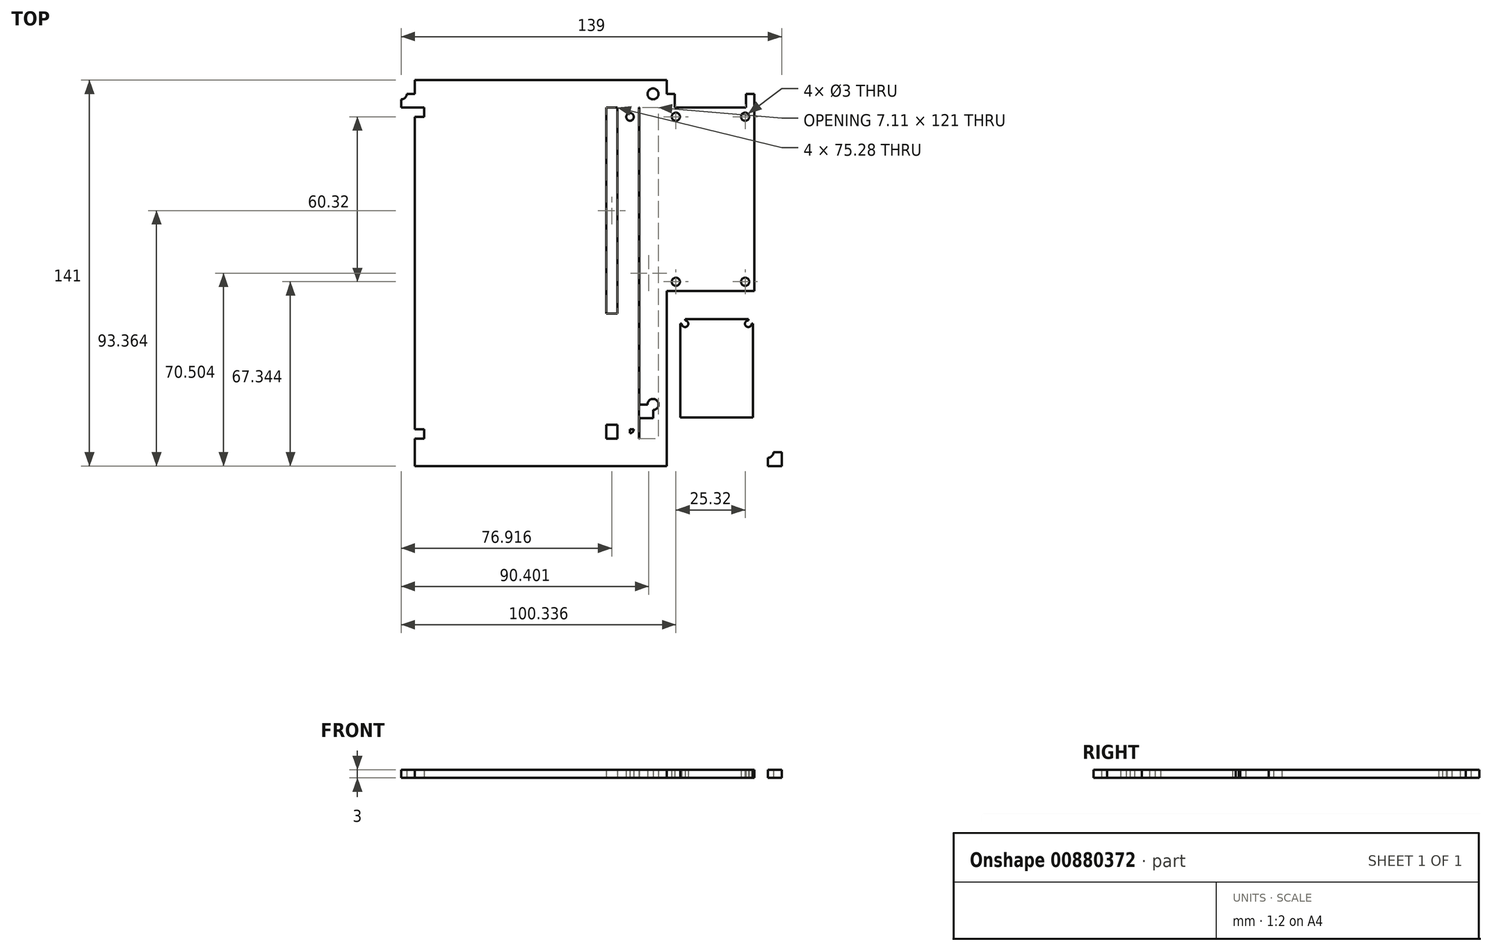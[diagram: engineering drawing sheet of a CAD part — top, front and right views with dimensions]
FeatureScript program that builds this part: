
annotation { "Feature Type Name" : "Feature", "Feature Type Description" : "" }
export const myFeature = defineFeature(function(context is Context, id is Id, definition is map)
    precondition{}
    {
        {
            var Q0;
            Q0=qCreatedBy(makeId("Top.planeOp"),FACE);
            var sketch = newSketch(context, id + "F0", { "sketchPlane" : qUnion([Q0])});
            skLineSegment(sketch, "E0.bottom", {"start": v(-139.34, -1.26) * mm, "end": v(-129.34, -1.26) * mm});
            skLineSegment(sketch, "E0.top", {"start": v(-139.34, -11.26) * mm, "end": v(-129.34, -11.26) * mm});
            skLineSegment(sketch, "E0.left", {"start": v(-139.34, -1.26) * mm, "end": v(-139.34, -11.26) * mm});
            skLineSegment(sketch, "E0.right", {"start": v(-129.34, -1.26) * mm, "end": v(-129.34, -11.26) * mm});
            skLineSegment(sketch, "E1.left", {"start": v(-129.34, -11.26) * mm, "end": v(-129.34, -114.76) * mm});
            skLineSegment(sketch, "E2.bottom", {"start": v(-124.34, -124.58) * mm, "end": v(-97.84, -124.58) * mm});
            skLineSegment(sketch, "E2.top", {"start": v(-124.34, -88.58) * mm, "end": v(-97.84, -88.58) * mm});
            skLineSegment(sketch, "E2.left", {"start": v(-124.34, -124.58) * mm, "end": v(-124.34, -88.58) * mm});
            skLineSegment(sketch, "E2.right", {"start": v(-97.84, -124.58) * mm, "end": v(-97.84, -88.58) * mm});
            skLineSegment(sketch, "E3.bottom", {"start": v(-129.34, -114.76) * mm, "end": v(-139.34, -114.76) * mm});
            skLineSegment(sketch, "E3.top", {"start": v(-129.34, -124.76) * mm, "end": v(-139.34, -124.76) * mm});
            skLineSegment(sketch, "E3.left", {"start": v(-129.34, -114.76) * mm, "end": v(-129.34, -124.76) * mm});
            skLineSegment(sketch, "E3.right", {"start": v(-139.34, -114.76) * mm, "end": v(-139.34, -124.76) * mm});
            skLineSegment(sketch, "E4", {"start": v(-129.34, -11.26) * mm, "end": v(-126, -11.26) * mm});
            skLineSegment(sketch, "E5.bottom", {"start": v(-129.34, -11.26) * mm, "end": v(-126.54, -11.26) * mm});
            skLineSegment(sketch, "E5.left", {"start": v(-129.34, -11.26) * mm, "end": v(-129.34, -14.06) * mm});
            skLineSegment(sketch, "E6.left", {"start": v(-129.34, -114.76) * mm, "end": v(-129.34, -111.76) * mm});
            skLineSegment(sketch, "E7.bottom", {"start": v(-97.84, -88.58) * mm, "end": v(-99.54, -88.58) * mm});
            skLineSegment(sketch, "E7.top", {"start": v(-97.84, -90.28) * mm, "end": v(-99.54, -90.28) * mm});
            skLineSegment(sketch, "E7.left", {"start": v(-97.84, -88.58) * mm, "end": v(-97.84, -90.28) * mm});
            skLineSegment(sketch, "E7.right", {"start": v(-99.54, -88.58) * mm, "end": v(-99.54, -90.28) * mm});
            skLineSegment(sketch, "E8.bottom", {"start": v(-124.34, -88.58) * mm, "end": v(-122.64, -88.58) * mm});
            skLineSegment(sketch, "E8.top", {"start": v(-124.34, -90.28) * mm, "end": v(-122.64, -90.28) * mm});
            skLineSegment(sketch, "E8.left", {"start": v(-124.34, -88.58) * mm, "end": v(-124.34, -90.28) * mm});
            skLineSegment(sketch, "E8.right", {"start": v(-122.64, -88.58) * mm, "end": v(-122.64, -90.28) * mm});
            skCircle(sketch, "E9", {"center": v(-122.64, -90.28) * mm, "radius": 1.2 * mm});
            skCircle(sketch, "E10", {"center": v(-99.54, -90.28) * mm, "radius": 1.2 * mm});
            skLineSegment(sketch, "E11.bottom", {"start": v(-139.34, -124.76) * mm, "end": v(-134.34, -124.76) * mm});
            skLineSegment(sketch, "E11.top", {"start": v(-139.34, -119.76) * mm, "end": v(-134.34, -119.76) * mm});
            skLineSegment(sketch, "E11.left", {"start": v(-139.34, -124.76) * mm, "end": v(-139.34, -119.76) * mm});
            skLineSegment(sketch, "E11.right", {"start": v(-134.34, -124.76) * mm, "end": v(-134.34, -119.76) * mm});
            skCircle(sketch, "E12", {"center": v(-134.34, -119.76) * mm, "radius": 2 * mm});
            skLineSegment(sketch, "E13.bottom", {"start": v(-139.34, -1.26) * mm, "end": v(-134.34, -1.26) * mm});
            skLineSegment(sketch, "E13.top", {"start": v(-139.34, -6.26) * mm, "end": v(-134.34, -6.26) * mm});
            skLineSegment(sketch, "E13.left", {"start": v(-139.34, -1.26) * mm, "end": v(-139.34, -6.26) * mm});
            skLineSegment(sketch, "E13.right", {"start": v(-134.34, -1.26) * mm, "end": v(-134.34, -6.26) * mm});
            skCircle(sketch, "E14", {"center": v(-134.34, -6.26) * mm, "radius": 2 * mm});
            skLineSegment(sketch, "E15.bottom", {"start": v(-129.34, -11.26) * mm, "end": v(-126.34, -11.26) * mm});
            skLineSegment(sketch, "E15.left", {"start": v(-129.34, -11.26) * mm, "end": v(-129.34, -27.96) * mm});
            skLineSegment(sketch, "E16.left", {"start": v(-129.34, -114.76) * mm, "end": v(-129.34, -108.76) * mm});
            skLineSegment(sketch, "E17.left", {"start": v(-129.34, -114.76) * mm, "end": v(-129.34, -27.46) * mm});
            skLineSegment(sketch, "E18.MirrorCS", {"start": v(-139.5, -132.26) * mm, "end": v(-139.5, -11.26) * mm});
            skLineSegment(sketch, "E19.MirrorCS", {"start": v(-221.34, -11.26) * mm, "end": v(-139.34, -11.26) * mm});
            skLineSegment(sketch, "E20.MirrorCS", {"start": v(-221.34, -132.26) * mm, "end": v(-139.34, -132.26) * mm});
            skCircle(sketch, "E21.MirrorC", {"center": v(-142.74, -128.86) * mm, "radius": 1.4 * mm});
            skCircle(sketch, "E22.MirrorC", {"center": v(-217.94, -128.86) * mm, "radius": 1.7 * mm});
            skCircle(sketch, "E23.MirrorC", {"center": v(-217.94, -14.66) * mm, "radius": 1.4 * mm});
            skCircle(sketch, "E24.MirrorC", {"center": v(-142.74, -14.66) * mm, "radius": 1.4 * mm});
            skLineSegment(sketch, "E25.MirrorCS", {"start": v(-142.74, -11.26) * mm, "end": v(-142.74, -14.66) * mm});
            skLineSegment(sketch, "E26.MirrorCS", {"start": v(-139.34, -14.66) * mm, "end": v(-142.74, -14.66) * mm});
            skLineSegment(sketch, "E27.MirrorCS", {"start": v(-217.94, -11.26) * mm, "end": v(-217.94, -14.66) * mm});
            skLineSegment(sketch, "E28.MirrorCS", {"start": v(-221.34, -14.66) * mm, "end": v(-217.94, -14.66) * mm});
            skLineSegment(sketch, "E29.MirrorCS", {"start": v(-142.74, -132.26) * mm, "end": v(-142.74, -128.86) * mm});
            skLineSegment(sketch, "E30.MirrorCS", {"start": v(-139.34, -128.86) * mm, "end": v(-142.74, -128.86) * mm});
            skLineSegment(sketch, "E31.MirrorCS", {"start": v(-221.34, -128.86) * mm, "end": v(-217.94, -128.86) * mm});
            skLineSegment(sketch, "E32.MirrorCS", {"start": v(-217.94, -132.26) * mm, "end": v(-217.94, -128.86) * mm});
            skLineSegment(sketch, "E33", {"start": v(-221.34, -11.26) * mm, "end": v(-221.34, -1.26) * mm});
            skLineSegment(sketch, "E34", {"start": v(-221.34, -132.26) * mm, "end": v(-221.34, -11.26) * mm});
            skLineSegment(sketch, "E35", {"start": v(-221.34, -132.26) * mm, "end": v(-231.5, -132.26) * mm});
            skLineSegment(sketch, "E36.bottom", {"start": v(-221.34, -132.26) * mm, "end": v(-231.34, -132.26) * mm});
            skLineSegment(sketch, "E36.top", {"start": v(-221.34, -142.26) * mm, "end": v(-231.34, -142.26) * mm});
            skLineSegment(sketch, "E36.left", {"start": v(-221.34, -132.26) * mm, "end": v(-221.34, -142.26) * mm});
            skLineSegment(sketch, "E36.right", {"start": v(-231.34, -132.26) * mm, "end": v(-231.34, -142.26) * mm});
            skLineSegment(sketch, "E37.bottom", {"start": v(-221.34, -142.26) * mm, "end": v(-139.34, -142.26) * mm});
            skLineSegment(sketch, "E37.left", {"start": v(-221.34, -142.26) * mm, "end": v(-221.34, -132.26) * mm});
            skLineSegment(sketch, "E38", {"start": v(-231.34, -132.26) * mm, "end": v(-231.34, -1.26) * mm});
            skLineSegment(sketch, "E39.bottom", {"start": v(-129.34, -124.76) * mm, "end": v(-139.2, -124.76) * mm});
            skLineSegment(sketch, "E39.top", {"start": v(-129.34, -142.26) * mm, "end": v(-139.34, -142.26) * mm});
            skLineSegment(sketch, "E39.left", {"start": v(-129.34, -124.76) * mm, "end": v(-129.34, -142.26) * mm});
            skLineSegment(sketch, "E40", {"start": v(-139.34, -142.26) * mm, "end": v(-139.5, -132.26) * mm});
            skLineSegment(sketch, "E41.bottom", {"start": v(-231.34, -142.26) * mm, "end": v(-226.34, -142.26) * mm});
            skLineSegment(sketch, "E41.top", {"start": v(-231.34, -137.4) * mm, "end": v(-226.34, -137.4) * mm});
            skLineSegment(sketch, "E41.left", {"start": v(-231.34, -142.26) * mm, "end": v(-231.34, -137.4) * mm});
            skLineSegment(sketch, "E41.right", {"start": v(-226.34, -142.26) * mm, "end": v(-226.34, -137.4) * mm});
            skCircle(sketch, "E42", {"center": v(-226.34, -137.4) * mm, "radius": 2 * mm});
            skLineSegment(sketch, "E43.bottom", {"start": v(-221.34, -11.26) * mm, "end": v(-226.34, -11.26) * mm});
            skLineSegment(sketch, "E43.top", {"start": v(-221.34, -6.26) * mm, "end": v(-226.34, -6.26) * mm});
            skLineSegment(sketch, "E43.left", {"start": v(-221.34, -11.26) * mm, "end": v(-221.34, -6.26) * mm});
            skLineSegment(sketch, "E43.right", {"start": v(-226.34, -11.26) * mm, "end": v(-226.34, -6.26) * mm});
            skCircle(sketch, "E44", {"center": v(-226.34, -6.26) * mm, "radius": 2 * mm});
            skLineSegment(sketch, "E45.bottom", {"start": v(-129.34, -142.26) * mm, "end": v(-87.34, -142.26) * mm});
            skLineSegment(sketch, "E45.left", {"start": v(-129.34, -142.26) * mm, "end": v(-129.34, -114.76) * mm});
            skLineSegment(sketch, "E46.bottom", {"start": v(-139.34, -132.26) * mm, "end": v(-151.42, -132.26) * mm});
            skLineSegment(sketch, "E46.top", {"start": v(-139.34, -11.26) * mm, "end": v(-151.42, -11.26) * mm});
            skLineSegment(sketch, "E46.left", {"start": v(-139.34, -132.26) * mm, "end": v(-139.34, -11.26) * mm});
            skLineSegment(sketch, "E46.right", {"start": v(-151.42, -132.26) * mm, "end": v(-151.42, -11.26) * mm});
            skLineSegment(sketch, "E47.bottom", {"start": v(-151.42, -132.26) * mm, "end": v(-147.42, -132.26) * mm});
            skLineSegment(sketch, "E47.top", {"start": v(-151.42, -11.26) * mm, "end": v(-147.42, -11.26) * mm});
            skLineSegment(sketch, "E47.right", {"start": v(-147.42, -132.26) * mm, "end": v(-147.42, -11.26) * mm});
            skLineSegment(sketch, "E48.top", {"start": v(-151.42, -127.18) * mm, "end": v(-147.42, -127.18) * mm});
            skLineSegment(sketch, "E48.left", {"start": v(-151.42, -132.26) * mm, "end": v(-151.42, -127.18) * mm});
            skLineSegment(sketch, "E48.right", {"start": v(-147.42, -132.26) * mm, "end": v(-147.42, -127.18) * mm});
            skLineSegment(sketch, "E49.top", {"start": v(-151.42, -86.54) * mm, "end": v(-147.42, -86.54) * mm});
            skLineSegment(sketch, "E49.left", {"start": v(-151.42, -127.18) * mm, "end": v(-151.42, -86.54) * mm});
            skLineSegment(sketch, "E49.right", {"start": v(-147.42, -127.18) * mm, "end": v(-147.42, -86.54) * mm});
            skLineSegment(sketch, "E50.bottom", {"start": v(-129.34, -11.26) * mm, "end": v(-97.34, -11.26) * mm});
            skLineSegment(sketch, "E50.top", {"start": v(-129.34, -78.26) * mm, "end": v(-97.34, -78.26) * mm});
            skLineSegment(sketch, "E50.left", {"start": v(-129.34, -11.26) * mm, "end": v(-129.34, -78.26) * mm});
            skLineSegment(sketch, "E50.right", {"start": v(-97.34, -11.26) * mm, "end": v(-97.34, -78.26) * mm});
            skLineSegment(sketch, "E51.bottom", {"start": v(-129.34, -78.26) * mm, "end": v(-126, -78.26) * mm});
            skLineSegment(sketch, "E51.left", {"start": v(-129.34, -78.26) * mm, "end": v(-129.34, -74.92) * mm});
            skLineSegment(sketch, "E52.bottom", {"start": v(-97.34, -78.26) * mm, "end": v(-100.68, -78.26) * mm});
            skLineSegment(sketch, "E52.left", {"start": v(-97.34, -78.26) * mm, "end": v(-97.34, -74.92) * mm});
            skLineSegment(sketch, "E53.left", {"start": v(-129.34, -11.26) * mm, "end": v(-129.34, -14.6) * mm});
            skLineSegment(sketch, "E54.bottom", {"start": v(-97.34, -11.26) * mm, "end": v(-100.68, -11.26) * mm});
            skLineSegment(sketch, "E54.left", {"start": v(-97.34, -11.26) * mm, "end": v(-97.34, -14.6) * mm});
            skCircle(sketch, "E55", {"center": v(-126, -74.92) * mm, "radius": 1.5 * mm});
            skCircle(sketch, "E56", {"center": v(-100.68, -74.92) * mm, "radius": 1.5 * mm});
            skCircle(sketch, "E57", {"center": v(-100.68, -14.6) * mm, "radius": 1.5 * mm});
            skCircle(sketch, "E58", {"center": v(-126, -14.6) * mm, "radius": 1.5 * mm});
            skLineSegment(sketch, "E59", {"start": v(-231.34, -1.26) * mm, "end": v(-139.34, -1.26) * mm});
            skLineSegment(sketch, "E60", {"start": v(-87.34, -1.26) * mm, "end": v(-87.34, -142.26) * mm});
            skLineSegment(sketch, "E61.top", {"start": v(-129.34, -6.26) * mm, "end": v(-97.34, -6.26) * mm});
            skLineSegment(sketch, "E61.left", {"start": v(-129.34, -11.26) * mm, "end": v(-129.34, -6.26) * mm});
            skLineSegment(sketch, "E61.right", {"start": v(-97.34, -11.26) * mm, "end": v(-97.34, -6.26) * mm});
            skLineSegment(sketch, "E62", {"start": v(-87.34, -1.26) * mm, "end": v(-129.34, -1.26) * mm});
            skLineSegment(sketch, "E63.top", {"start": v(-129.34, -6.26) * mm, "end": v(-126.34, -6.26) * mm});
            skLineSegment(sketch, "E63.right", {"start": v(-126.34, -11.26) * mm, "end": v(-126.34, -6.26) * mm});
            skLineSegment(sketch, "E64.right", {"start": v(-97.34, -11.26) * mm, "end": v(-97.34, -11.26) * mm});
            skLineSegment(sketch, "E65.bottom", {"start": v(-97.34, -11.26) * mm, "end": v(-100.34, -11.26) * mm});
            skLineSegment(sketch, "E65.top", {"start": v(-97.34, -6.26) * mm, "end": v(-100.34, -6.26) * mm});
            skLineSegment(sketch, "E65.right", {"start": v(-100.34, -11.26) * mm, "end": v(-100.34, -6.26) * mm});
            skLineSegment(sketch, "E66.bottom", {"start": v(-87.34, -142.26) * mm, "end": v(-92.34, -142.26) * mm});
            skLineSegment(sketch, "E66.top", {"start": v(-87.34, -137.26) * mm, "end": v(-92.34, -137.26) * mm});
            skLineSegment(sketch, "E66.left", {"start": v(-87.34, -142.26) * mm, "end": v(-87.34, -137.26) * mm});
            skLineSegment(sketch, "E66.right", {"start": v(-92.34, -142.26) * mm, "end": v(-92.34, -137.26) * mm});
            skLineSegment(sketch, "E67.bottom", {"start": v(-87.34, -1.26) * mm, "end": v(-92.34, -1.26) * mm});
            skLineSegment(sketch, "E67.top", {"start": v(-87.34, -6.26) * mm, "end": v(-92.34, -6.26) * mm});
            skLineSegment(sketch, "E67.left", {"start": v(-87.34, -1.26) * mm, "end": v(-87.34, -6.26) * mm});
            skLineSegment(sketch, "E67.right", {"start": v(-92.34, -1.26) * mm, "end": v(-92.34, -6.26) * mm});
            skCircle(sketch, "E68", {"center": v(-92.34, -137.26) * mm, "radius": 2 * mm});
            skCircle(sketch, "E69", {"center": v(-92.34, -6.26) * mm, "radius": 2 * mm});
            skSolve(sketch);
        }
        {
            var Q0;
            Q0=makeQuery(id+"F0.imprint","IMPRINT",FACE,{"disambiguationData":[TD([[makeQuery(id+"F0.imprint","IMPRINT",EDGE,{"derivedFrom":sQuery(id+"F0.wireOp",EDGE,"E1.right")}),1.0]])]});
            var Q1;
            Q1=makeQuery(id+"F0.imprint","IMPRINT",FACE,{"disambiguationData":[TD([[makeQuery(id+"F0.imprint","IMPRINT",EDGE,{"derivedFrom":sQuery(id+"F0.wireOp",EDGE,"5LbS737s-GMt0-3yRV-RusY-74rPWMoJnLPp.bottom")}),-1.0]])]});
            var Q2;
            Q2=makeQuery(id+"F0.imprint","IMPRINT",FACE,{"disambiguationData":[TD([[makeQuery(id+"F0.imprint","IMPRINT",EDGE,{"derivedFrom":sQuery(id+"F0.wireOp",EDGE,"E1.top")}),-1.0]])]});
            var Q3;
            Q3=makeQuery(id+"F0.imprint","IMPRINT",FACE,{"disambiguationData":[TD([[makeQuery(id+"F0.imprint","IMPRINT",EDGE,{"derivedFrom":sQuery(id+"F0.wireOp",EDGE,"E3.bottom")}),1.0]])]});
            var Q4;
            Q4=makeQuery(id+"F0.imprint","IMPRINT",FACE,{"disambiguationData":[TD([[makeQuery(id+"F0.imprint","IMPRINT",EDGE,{"derivedFrom":sQuery(id+"F0.wireOp",EDGE,"97myMdQA-agTY-EE5a-eSU0-3Ky6piHqa90I.left")}),1.0]])]});
            var Q5;
            Q5=makeQuery(id+"F0.imprint","IMPRINT",FACE,{"disambiguationData":[TD([[makeQuery(id+"F0.imprint","IMPRINT",EDGE,{"derivedFrom":sQuery(id+"F0.wireOp",EDGE,"E0.bottom")}),-1.0]])]});
            var Q6;
            {var subQ0=sQuery(id+"F0.wireOp",EDGE,"E0.right");Q6=makeQuery(id+"F0.imprint","IMPRINT",FACE,{"disambiguationData":[TD([[makeQuery(id+"F0.imprint","IMPRINT",EDGE,{"derivedFrom":subQ0}),1.0]])]});}
            var Q7;
            {var subQ2=sQuery(id+"F0.wireOp",EDGE,"97myMdQA-agTY-EE5a-eSU0-3Ky6piHqa90I.right");Q7=makeQuery(id+"F0.imprint","IMPRINT",FACE,{"disambiguationData":[TD([[makeQuery(id+"F0.imprint","IMPRINT",EDGE,{"derivedFrom":subQ2}),-1.0]])]});}
            var Q8;
            {var subQ0=sQuery(id+"F0.wireOp",EDGE,"5LbS737s-GMt0-3yRV-RusY-74rPWMoJnLPp.top");Q8=makeQuery(id+"F0.imprint","IMPRINT",FACE,{"disambiguationData":[TD([[makeQuery(id+"F0.imprint","IMPRINT",EDGE,{"derivedFrom":subQ0}),-1.0]])]});}
            var Q9;
            {var subQ1=sQuery(id+"F0.wireOp",EDGE,"R2WY0SRa-AH7d-UwmP-SjNj-uamWJIKeu4LY.bottom");Q9=makeQuery(id+"F0.imprint","IMPRINT",FACE,{"disambiguationData":[TD([[makeQuery(id+"F0.imprint","IMPRINT",EDGE,{"derivedFrom":subQ1}),1.0]])]});}
            var Q10;
            {var subQ1=sQuery(id+"F0.wireOp",EDGE,"E11.bottom");Q10=makeQuery(id+"F0.imprint","IMPRINT",FACE,{"disambiguationData":[TD([[makeQuery(id+"F0.imprint","IMPRINT",EDGE,{"derivedFrom":subQ1}),1.0]])]});}
            var Q11;
            {var subQ1=sQuery(id+"F0.wireOp",EDGE,"E13.bottom");Q11=makeQuery(id+"F0.imprint","IMPRINT",FACE,{"disambiguationData":[TD([[makeQuery(id+"F0.imprint","IMPRINT",EDGE,{"derivedFrom":subQ1}),-1.0]])]});}
            var Q12;
            {var subQ1=sQuery(id+"F0.wireOp",EDGE,"GQXUHQXK-ggnU-ynUD-V26a-dyRAC2FfGFxX.bottom");Q12=makeQuery(id+"F0.imprint","IMPRINT",FACE,{"disambiguationData":[TD([[makeQuery(id+"F0.imprint","IMPRINT",EDGE,{"derivedFrom":subQ1}),1.0]])]});}
            var Q13;
            {var subQ1=sQuery(id+"F0.wireOp",EDGE,"E39.top");Q13=makeQuery(id+"F0.imprint","IMPRINT",FACE,{"disambiguationData":[TD([[makeQuery(id+"F0.imprint","IMPRINT",EDGE,{"derivedFrom":subQ1}),-1.0]])]});}
            var Q14;
            Q14=makeQuery(id+"F0.imprint","IMPRINT",FACE,{"disambiguationData":[TD([[makeQuery(id+"F0.imprint","IMPRINT",EDGE,{"derivedFrom":sQuery(id+"F0.wireOp",EDGE,"E36.bottom")}),1.0]])]});
            var Q15;
            {var subQ4=sQuery(id+"F0.wireOp",EDGE,"E33");Q15=makeQuery(id+"F0.imprint","IMPRINT",FACE,{"disambiguationData":[TD([[makeQuery(id+"F0.imprint","IMPRINT",EDGE,{"derivedFrom":subQ4}),1.0]])]});}
            var Q16;
            {var subQ12=sQuery(id+"F0.wireOp",EDGE,"E0.top");Q16=makeQuery(id+"F0.imprint","IMPRINT",FACE,{"disambiguationData":[TD([[makeQuery(id+"F0.imprint","IMPRINT",EDGE,{"derivedFrom":subQ12}),-1.0]])]});}
            var Q17;
            {var subQ5=sQuery(id+"F0.wireOp",EDGE,"E0.top");Q17=makeQuery(id+"F0.imprint","IMPRINT",FACE,{"disambiguationData":[TD([[makeQuery(id+"F0.imprint","IMPRINT",EDGE,{"derivedFrom":subQ5}),1.0]])]});}
            var Q18;
            Q18=makeQuery(id+"F0.imprint","IMPRINT",FACE,{"disambiguationData":[TD([[makeQuery(id+"F0.imprint","IMPRINT",EDGE,{"derivedFrom":sQuery(id+"F0.wireOp",EDGE,"OHmSuH0F-fEJm-if1A-v7VG-6K46aT4ydrlh")}),1.0]])]});
            var Q19;
            {var subQ5=sQuery(id+"F0.wireOp",EDGE,"E13.left");Q19=makeQuery(id+"F0.imprint","IMPRINT",FACE,{"disambiguationData":[TD([[makeQuery(id+"F0.imprint","IMPRINT",EDGE,{"derivedFrom":subQ5}),1.0]])]});}
            var Q20;
            {var subQ1=sQuery(id+"F0.wireOp",EDGE,"E41.bottom");Q20=makeQuery(id+"F0.imprint","IMPRINT",FACE,{"disambiguationData":[TD([[makeQuery(id+"F0.imprint","IMPRINT",EDGE,{"derivedFrom":subQ1}),1.0]])]});}
            var Q21;
            {var subQ1=sQuery(id+"F0.wireOp",EDGE,"yvfpG27f-ZHmC-TrTi-RBKr-novi9orWfjoi.bottom");Q21=makeQuery(id+"F0.imprint","IMPRINT",FACE,{"disambiguationData":[TD([[makeQuery(id+"F0.imprint","IMPRINT",EDGE,{"derivedFrom":subQ1}),-1.0]])]});}
            var Q22;
            {var subQ1=sQuery(id+"F0.wireOp",EDGE,"E43.bottom");Q22=makeQuery(id+"F0.imprint","IMPRINT",FACE,{"disambiguationData":[TD([[makeQuery(id+"F0.imprint","IMPRINT",EDGE,{"derivedFrom":subQ1}),-1.0]])]});}
            var Q23;
            Q23=makeQuery(id+"F0.imprint","IMPRINT",FACE,{"disambiguationData":[TD([[makeQuery(id+"F0.imprint","IMPRINT",EDGE,{"derivedFrom":sQuery(id+"F0.wireOp",EDGE,"E37.bottom")}),1.0]])]});
            var Q24;
            {var subQ5=sQuery(id+"F0.wireOp",EDGE,"E45.bottom");Q24=makeQuery(id+"F0.imprint","IMPRINT",FACE,{"disambiguationData":[TD([[makeQuery(id+"F0.imprint","IMPRINT",EDGE,{"derivedFrom":subQ5}),1.0]])]});}
            var Q25;
            {var subQ0=sQuery(id+"F0.wireOp",EDGE,"E45.right");var subQ6=sQuery(id+"F0.wireOp",EDGE,"ZUBNZQG8-KCI5-j7Eh-KT8m-DHS590PrAmv4.top");var subQ8=makeQuery(id+"F0.imprint","INTERSECT",VERTEX,{"derivedFrom":[subQ6,subQ0]});Q25=makeQuery(id+"F0.imprint","IMPRINT",FACE,{"disambiguationData":[TD([[makeQuery(id+"F0.imprint","IMPRINT",EDGE,{"disambiguationData":[TD([[subQ8,-1.0]])],"derivedFrom":subQ6}),-1.0]])]});}
            var Q26;
            {var subQ5=sQuery(id+"F0.wireOp",EDGE,"vMtd8N3i-DgQX-cZyN-V79B-nuaA6O4M76Ab");Q26=makeQuery(id+"F0.imprint","IMPRINT",FACE,{"disambiguationData":[TD([[makeQuery(id+"F0.imprint","IMPRINT",EDGE,{"derivedFrom":subQ5}),-1.0]])]});}
            var Q27;
            {var subQ3=sQuery(id+"F0.wireOp",EDGE,"ss2Z4Fs3-Muc6-eGxa-EgVp-308dcmax2r1z.right");var subQ5=sQuery(id+"F0.wireOp",EDGE,"ss2Z4Fs3-Muc6-eGxa-EgVp-308dcmax2r1z.bottom");var subQ7=makeQuery(id+"F0.imprint","INTERSECT",VERTEX,{"derivedFrom":[subQ5,subQ3]});Q27=makeQuery(id+"F0.imprint","IMPRINT",FACE,{"disambiguationData":[TD([[makeQuery(id+"F0.imprint","IMPRINT",EDGE,{"disambiguationData":[TD([[subQ7,-1.0]])],"derivedFrom":subQ3}),1.0]])]});}
            var Q28;
            Q28=makeQuery(id+"F0.imprint","IMPRINT",FACE,{"disambiguationData":[TD([[makeQuery(id+"F0.imprint","IMPRINT",EDGE,{"derivedFrom":sQuery(id+"F0.wireOp",EDGE,"BjaOcRhM-ncdW-A79u-4p9Y-5Tw2Hmfoguzv.top")}),1.0]])]});
            var Q29;
            {var subQ5=sQuery(id+"F0.wireOp",EDGE,"GQXUHQXK-ggnU-ynUD-V26a-dyRAC2FfGFxX.left");Q29=makeQuery(id+"F0.imprint","IMPRINT",FACE,{"disambiguationData":[TD([[makeQuery(id+"F0.imprint","IMPRINT",EDGE,{"derivedFrom":subQ5}),-1.0]])]});}
            var Q30;
            {var subQ0=sQuery(id+"F0.wireOp",EDGE,"ZUBNZQG8-KCI5-j7Eh-KT8m-DHS590PrAmv4.top");Q30=makeQuery(id+"F0.imprint","IMPRINT",FACE,{"disambiguationData":[TD([[makeQuery(id+"F0.imprint","IMPRINT",EDGE,{"derivedFrom":subQ0}),1.0]])]});}
            var Q31;
            Q31=makeQuery(id+"F0.imprint","IMPRINT",FACE,{"disambiguationData":[TD([[makeQuery(id+"F0.imprint","IMPRINT",EDGE,{"derivedFrom":sQuery(id+"F0.wireOp",EDGE,"HVovfB2P-Sk3F-LjXf-JXG4-bCGlqA5Mxosq.bottom")}),1.0]])]});
            var Q32;
            Q32=makeQuery(id+"F0.imprint","IMPRINT",FACE,{"disambiguationData":[TD([[makeQuery(id+"F0.imprint","IMPRINT",EDGE,{"derivedFrom":sQuery(id+"F0.wireOp",EDGE,"E63.top")}),-1.0]])]});
            var Q33;
            Q33=makeQuery(id+"F0.imprint","IMPRINT",FACE,{"disambiguationData":[TD([[makeQuery(id+"F0.imprint","IMPRINT",EDGE,{"derivedFrom":sQuery(id+"F0.wireOp",EDGE,"E65.bottom")}),-1.0]])]});
            var Q34;
            {var subQ1=sQuery(id+"F0.wireOp",EDGE,"E66.bottom");Q34=makeQuery(id+"F0.imprint","IMPRINT",FACE,{"disambiguationData":[TD([[makeQuery(id+"F0.imprint","IMPRINT",EDGE,{"derivedFrom":subQ1}),-1.0]])]});}
            var Q35;
            {var subQ1=sQuery(id+"F0.wireOp",EDGE,"E67.bottom");Q35=makeQuery(id+"F0.imprint","IMPRINT",FACE,{"disambiguationData":[TD([[makeQuery(id+"F0.imprint","IMPRINT",EDGE,{"derivedFrom":subQ1}),1.0]])]});}
            var Q36;
            {var subQ0=sQuery(id+"F0.wireOp",EDGE,"E46.right");Q36=makeQuery(id+"F0.imprint","IMPRINT",FACE,{"disambiguationData":[TD([[makeQuery(id+"F0.imprint","IMPRINT",EDGE,{"derivedFrom":subQ0}),1.0]])]});}
            var Q37;
            {var subQ7=sQuery(id+"F0.wireOp",EDGE,"E0.left");Q37=makeQuery(id+"F0.imprint","IMPRINT",FACE,{"disambiguationData":[TD([[makeQuery(id+"F0.imprint","IMPRINT",EDGE,{"derivedFrom":subQ7}),-1.0]])]});}
            var Q38;
            Q38=makeQuery(id+"F0.imprint","IMPRINT",FACE,{"disambiguationData":[TD([[makeQuery(id+"F0.imprint","IMPRINT",EDGE,{"derivedFrom":sQuery(id+"F0.wireOp",EDGE,"E47.top")}),-1.0]])]});
            var Q39;
            Q39=makeQuery(id+"F0.imprint","IMPRINT",FACE,{"disambiguationData":[TD([[makeQuery(id+"F0.imprint","IMPRINT",EDGE,{"derivedFrom":sQuery(id+"F0.wireOp",EDGE,"E48.top")}),1.0]])]});
            var Q40;
            Q40=makeQuery(id+"F0.imprint","IMPRINT",FACE,{"disambiguationData":[TD([[makeQuery(id+"F0.imprint","IMPRINT",EDGE,{"derivedFrom":sQuery(id+"F0.wireOp",EDGE,"E47.bottom")}),1.0]])]});
            var Q41;
            {var subQ0=sQuery(id+"F0.wireOp",EDGE,"E47.right");Q41=makeQuery(id+"F0.imprint","IMPRINT",FACE,{"disambiguationData":[TD([[makeQuery(id+"F0.imprint","IMPRINT",EDGE,{"derivedFrom":subQ0}),-1.0]])]});}
            var Q42;
            Q42=makeQuery(id+"F0.imprint","IMPRINT",FACE,{"disambiguationData":[TD([[makeQuery(id+"F0.imprint","IMPRINT",EDGE,{"derivedFrom":sQuery(id+"F0.wireOp",EDGE,"E2.bottom")}),1.0]])]});
            var Q43;
            Q43=makeQuery(id+"F0.imprint","IMPRINT",FACE,{"disambiguationData":[TD([[makeQuery(id+"F0.imprint","IMPRINT",EDGE,{"derivedFrom":sQuery(id+"F0.wireOp",EDGE,"E50.top")}),1.0]])]});
            var Q44;
            Q44=makeQuery(id+"F0.imprint","IMPRINT",FACE,{"disambiguationData":[TD([[makeQuery(id+"F0.imprint","IMPRINT",EDGE,{"derivedFrom":sQuery(id+"F0.wireOp",EDGE,"E61.top")}),-1.0]])]});
            var Q45;
            {var subQ0=sQuery(id+"F0.wireOp",EDGE,"E46.top");var subQ5=sQuery(id+"F0.wireOp",EDGE,"E18.MirrorCS");var subQ6=makeQuery(id+"F0.imprint","INTERSECT",VERTEX,{"derivedFrom":[subQ5,subQ0]});Q45=makeQuery(id+"F0.imprint","IMPRINT",FACE,{"disambiguationData":[TD([[makeQuery(id+"F0.imprint","IMPRINT",EDGE,{"disambiguationData":[TD([[subQ6,1.0]])],"derivedFrom":subQ5}),1.0]])]});}
            var Q46;
            {var subQ3=sQuery(id+"F0.wireOp",EDGE,"E23.MirrorC");var subQ5=sQuery(id+"F0.wireOp",EDGE,"E27.MirrorCS");var subQ6=makeQuery(id+"F0.imprint","INTERSECT",VERTEX,{"derivedFrom":[subQ3,subQ5]});Q46=makeQuery(id+"F0.imprint","IMPRINT",FACE,{"disambiguationData":[TD([[makeQuery(id+"F0.imprint","IMPRINT",EDGE,{"disambiguationData":[TD([[subQ6,1.0]])],"derivedFrom":subQ3}),1.0]])]});}
            var Q47;
            {var subQ3=sQuery(id+"F0.wireOp",EDGE,"E22.MirrorC");var subQ6=sQuery(id+"F0.wireOp",EDGE,"E31.MirrorCS");var subQ9=makeQuery(id+"F0.imprint","INTERSECT",VERTEX,{"derivedFrom":[subQ3,subQ6]});Q47=makeQuery(id+"F0.imprint","IMPRINT",FACE,{"disambiguationData":[TD([[makeQuery(id+"F0.imprint","IMPRINT",EDGE,{"disambiguationData":[TD([[subQ9,1.0]])],"derivedFrom":subQ3}),1.0]])]});}
            var Q48;
            {var subQ1=sQuery(id+"F0.wireOp",EDGE,"E29.MirrorCS");var subQ3=sQuery(id+"F0.wireOp",EDGE,"E21.MirrorC");var subQ4=makeQuery(id+"F0.imprint","INTERSECT",VERTEX,{"derivedFrom":[subQ3,subQ1]});Q48=makeQuery(id+"F0.imprint","IMPRINT",FACE,{"disambiguationData":[TD([[makeQuery(id+"F0.imprint","IMPRINT",EDGE,{"disambiguationData":[TD([[subQ4,1.0]])],"derivedFrom":subQ3}),1.0]])]});}
            var Q49;
            {var subQ1=sQuery(id+"F0.wireOp",EDGE,"E8.bottom");Q49=makeQuery(id+"F0.imprint","IMPRINT",FACE,{"disambiguationData":[TD([[makeQuery(id+"F0.imprint","IMPRINT",EDGE,{"derivedFrom":subQ1}),-1.0]])]});}
            var Q50;
            {var subQ1=sQuery(id+"F0.wireOp",EDGE,"E7.bottom");Q50=makeQuery(id+"F0.imprint","IMPRINT",FACE,{"disambiguationData":[TD([[makeQuery(id+"F0.imprint","IMPRINT",EDGE,{"derivedFrom":subQ1}),1.0]])]});}
            extrude(context, id + "F1", {"entities" : qUnion([Q0, Q1, Q2, Q3, Q4, Q5, Q6, Q7, Q8, Q9, Q10, Q11, Q12, Q13, Q14, Q15, Q16, Q17, Q18, Q19, Q20, Q21, Q22, Q23, Q24, Q25, Q26, Q27, Q28, Q29, Q30, Q31, Q32, Q33, Q34, Q35, Q36, Q37, Q38, Q39, Q40, Q41, Q42, Q43, Q44, Q45, Q46, Q47, Q48, Q49, Q50]), "depth" : 3 * mm, "offsetDistance" : 25 * mm});
        }
    });
